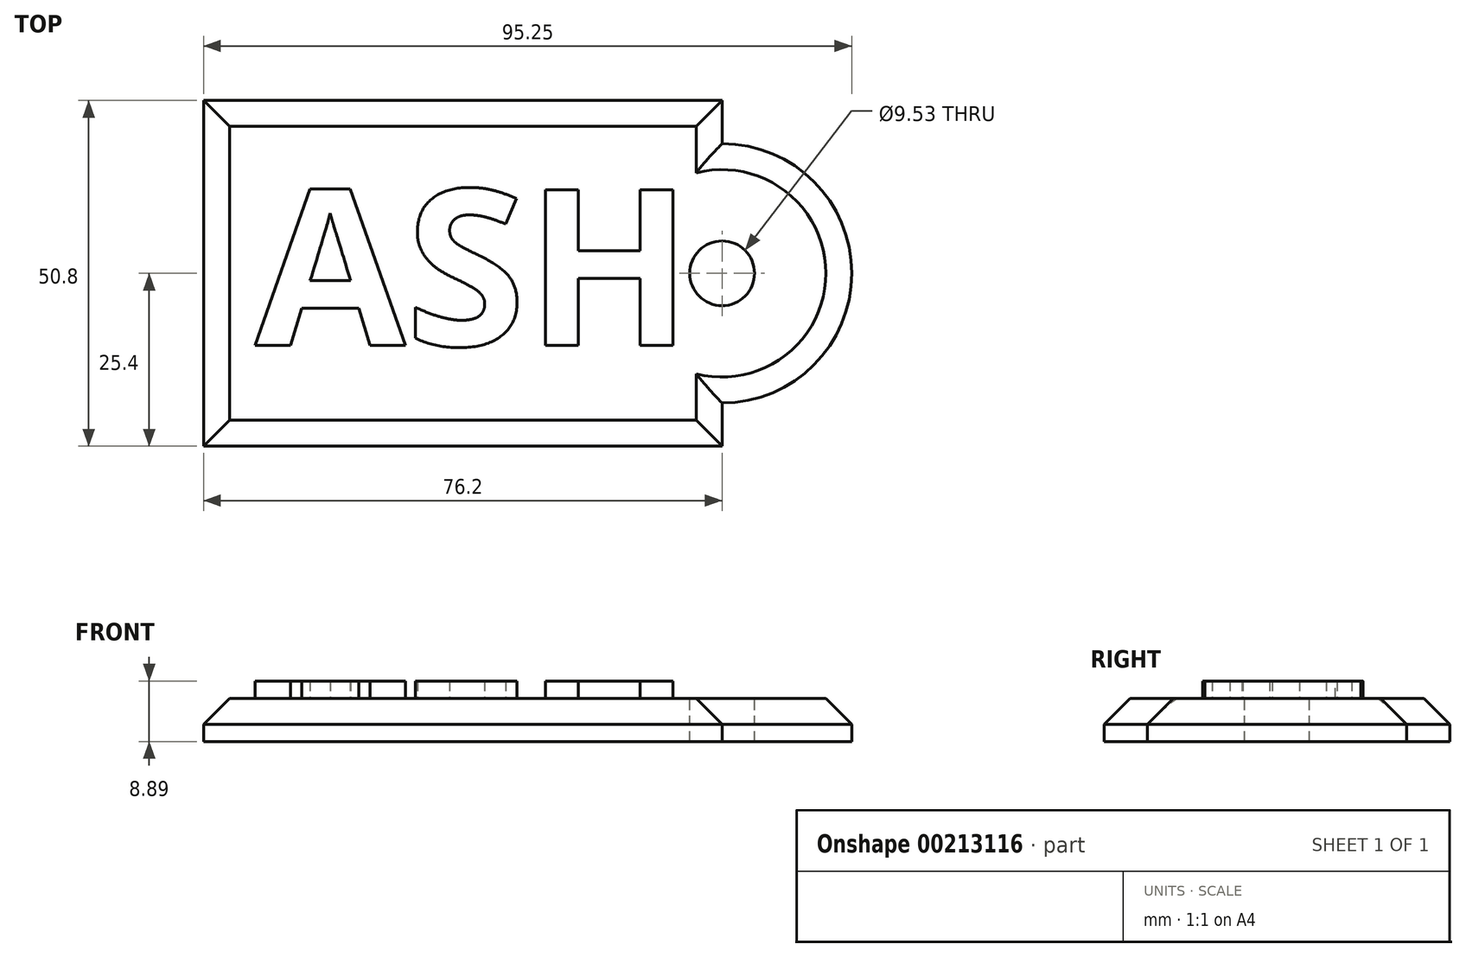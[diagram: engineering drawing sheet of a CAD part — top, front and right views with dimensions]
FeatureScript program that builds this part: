
annotation { "Feature Type Name" : "Feature", "Feature Type Description" : "" }
export const myFeature = defineFeature(function(context is Context, id is Id, definition is map)
    precondition{}
    {
        {
            var Q0;
            Q0=qCreatedBy(makeId("Top.planeOp"),FACE);
            var sketch = newSketch(context, id + "F0", { "sketchPlane" : qUnion([Q0])});
            skLineSegment(sketch, "E0.bottom", {"start": v(0, 0) * mm, "end": v(76.2, 0) * mm});
            skLineSegment(sketch, "E0.top", {"start": v(0, 50.8) * mm, "end": v(76.2, 50.8) * mm});
            skLineSegment(sketch, "E0.left", {"start": v(0, 0) * mm, "end": v(0, 50.8) * mm});
            skLineSegment(sketch, "E0.right", {"start": v(76.2, 0) * mm, "end": v(76.2, 50.8) * mm});
            skSolve(sketch);
        }
        {
            var Q0;
            Q0=makeQuery(id+"F0.imprint","IMPRINT",FACE,{"disambiguationData":[TD([[makeQuery(id+"F0.imprint","IMPRINT",EDGE,{"derivedFrom":sQuery(id+"F0.wireOp",EDGE,"E0.bottom")}),1.0]])]});
            extrude(context, id + "F1", {"entities" : qUnion([Q0]), "depth" : 6.35 * mm});
        }
        {
            var Q0;
            Q0=makeQuery(id+"F1.opExtrude","CAP_FACE",FACE,{"disambiguationData":[OSD([sQuery(id+"F0.wireOp",EDGE,"E0.bottom"),sQuery(id+"F0.wireOp",EDGE,"E0.top"),sQuery(id+"F0.wireOp",EDGE,"E0.left"),sQuery(id+"F0.wireOp",EDGE,"E0.right")])],"isStart":false});
            var sketch = newSketch(context, id + "F2", { "sketchPlane" : qUnion([Q0])});
            skCircle(sketch, "E1", {"center": v(76.2, 25.4) * mm, "radius": 19.05 * mm});
            skSolve(sketch);
        }
        {
            var Q0;
            {var subQ0=sQuery(id+"F2.wireOp",EDGE,"E1");var subQ1=makeQuery(id+"F1.opExtrude","CAP_EDGE",EDGE,{"disambiguationData":[OSD([sQuery(id+"F0.wireOp",EDGE,"E0.right")])],"isStart":false});var subQ2=makeQuery(id+"F2.imprint","INTERSECT",VERTEX,{"disambiguationData":[OD(0.0)],"derivedFrom":[subQ1,subQ0]});Q0=makeQuery(id+"F2.imprint","IMPRINT",FACE,{"disambiguationData":[TD([[makeQuery(id+"F2.imprint","IMPRINT",EDGE,{"disambiguationData":[TD([[subQ2,-1.0]])],"derivedFrom":subQ0}),1.0]])]});}
            extrude(context, id + "F3", {"entities" : qUnion([Q0]), "operationType" : NewBodyOperationType.ADD, "oppositeDirection" : true, "depth" : 6.35 * mm});
        }
        {
            var Q0;
            {var subQ0=sQuery(id+"F0.wireOp",EDGE,"E0.right");Q0=makeQuery(id+"F3.boolean.opBoolean","MERGE",FACE,{"derivedFrom":[makeQuery(id+"F1.opExtrude","CAP_FACE",FACE,{"disambiguationData":[OSD([sQuery(id+"F0.wireOp",EDGE,"E0.bottom"),sQuery(id+"F0.wireOp",EDGE,"E0.top"),sQuery(id+"F0.wireOp",EDGE,"E0.left"),subQ0])],"isStart":false}),makeQuery(id+"F3.opExtrude","CAP_FACE",FACE,{"disambiguationData":[OSD([subQ0,sQuery(id+"F2.wireOp",EDGE,"E1")])],"isStart":true})]});}
            var sketch = newSketch(context, id + "F4", { "sketchPlane" : qUnion([Q0])});
            skText(sketch, "E2", { "text": "ASH", "fontName": "OpenSans-Bold.ttf"});
            const initialGuessF4  = {"E2": [0.00755, 0.0148, 1, 0, 0.02309]};
            skSetInitialGuess(sketch, initialGuessF4);
            skSolve(sketch);
        }
        {
            var Q0;
            Q0 = qSketchRegion(id + "F4", true);
            extrude(context, id + "F5", {"entities" : qUnion([Q0]), "operationType" : NewBodyOperationType.ADD, "depth" : 2.54 * mm});
        }
        {
            var Q0;
            {var subQ0=sQuery(id+"F2.wireOp",EDGE,"E1");var subQ1=sQuery(id+"F0.wireOp",EDGE,"E0.top");var subQ2=sQuery(id+"F0.wireOp",EDGE,"E0.bottom");var subQ3=sQuery(id+"F0.wireOp",EDGE,"E0.left");var subQ4=sQuery(id+"F0.wireOp",EDGE,"E0.right");Q0=makeQuery(id+"F5.boolean.opBoolean","SPLIT",FACE,{"disambiguationData":[TD([makeQuery(id+"F1.opExtrude","SWEPT_FACE",FACE,{"disambiguationData":[OSD([subQ2])]})])],"derivedFrom":makeQuery(id+"F3.boolean.opBoolean","MERGE",FACE,{"derivedFrom":[makeQuery(id+"F1.opExtrude","CAP_FACE",FACE,{"disambiguationData":[OSD([subQ2,subQ1,subQ3,subQ4])],"isStart":false}),makeQuery(id+"F3.opExtrude","CAP_FACE",FACE,{"disambiguationData":[OSD([subQ4,subQ0])],"isStart":true})]})});}
            var sketch = newSketch(context, id + "F6", { "sketchPlane" : qUnion([Q0])});
            skPoint(sketch, "E3", {"position": v(76.2, 25.4) * mm});
            skSolve(sketch);
        }
        {
            var Q0;
            Q0=sQuery(id+"F6.wireOp",VERTEX,"E3");
            var Q1;
            Q1=makeQuery(id+"F1.opExtrude","SWEPT_BODY",BODY,{"disambiguationData":[OSD([sQuery(id+"F0.wireOp",EDGE,"E0.bottom"),sQuery(id+"F0.wireOp",EDGE,"E0.top"),sQuery(id+"F0.wireOp",EDGE,"E0.left"),sQuery(id+"F0.wireOp",EDGE,"E0.right")])]});
            hole(context, id + "F7", {"style" : HoleStyle.SIMPLE, "endStyle" : HoleEndStyle.THROUGH, "holeDiameter" : 9.52 * mm, "locations" : qUnion([Q0]), "scope" : qUnion([Q1]), "isTappedThrough" : true});
        }
        {
            var Q0;
            Q0=makeQuery(id+"F1.opExtrude","CAP_EDGE",EDGE,{"disambiguationData":[OSD([sQuery(id+"F0.wireOp",EDGE,"E0.left")])],"isStart":false});
            var Q1;
            Q1=makeQuery(id+"F1.opExtrude","CAP_EDGE",EDGE,{"disambiguationData":[OSD([sQuery(id+"F0.wireOp",EDGE,"E0.bottom")])],"isStart":false});
            var Q2;
            Q2=makeQuery(id+"F1.opExtrude","CAP_EDGE",EDGE,{"disambiguationData":[OSD([sQuery(id+"F0.wireOp",EDGE,"E0.top")])],"isStart":false});
            var Q3;
            {var subQ1=sQuery(id+"F0.wireOp",EDGE,"E0.right");var subQ2=sQuery(id+"F0.wireOp",EDGE,"E0.top");Q3=makeQuery(id+"F3.boolean.opBoolean","SPLIT",EDGE,{"disambiguationData":[TD([makeQuery(id+"F1.opExtrude","SWEPT_FACE",FACE,{"disambiguationData":[OSD([subQ2])]})])],"derivedFrom":makeQuery(id+"F1.opExtrude","CAP_EDGE",EDGE,{"disambiguationData":[OSD([subQ1])],"isStart":false})});}
            var Q4;
            Q4=makeQuery(id+"F3.opExtrude","CAP_EDGE",EDGE,{"disambiguationData":[OSD([sQuery(id+"F2.wireOp",EDGE,"E1")])],"isStart":true});
            var Q5;
            {var subQ0=sQuery(id+"F0.wireOp",EDGE,"E0.right");var subQ2=sQuery(id+"F0.wireOp",EDGE,"E0.bottom");Q5=makeQuery(id+"F3.boolean.opBoolean","SPLIT",EDGE,{"disambiguationData":[TD([makeQuery(id+"F1.opExtrude","SWEPT_FACE",FACE,{"disambiguationData":[OSD([subQ2])]})])],"derivedFrom":makeQuery(id+"F1.opExtrude","CAP_EDGE",EDGE,{"disambiguationData":[OSD([subQ0])],"isStart":false})});}
            chamfer(context, id + "F8", {"entities" : qUnion([Q0, Q1, Q2, Q3, Q4, Q5]), "width" : 3.8 * mm, "tangentPropagation" : true});
        }
    });
